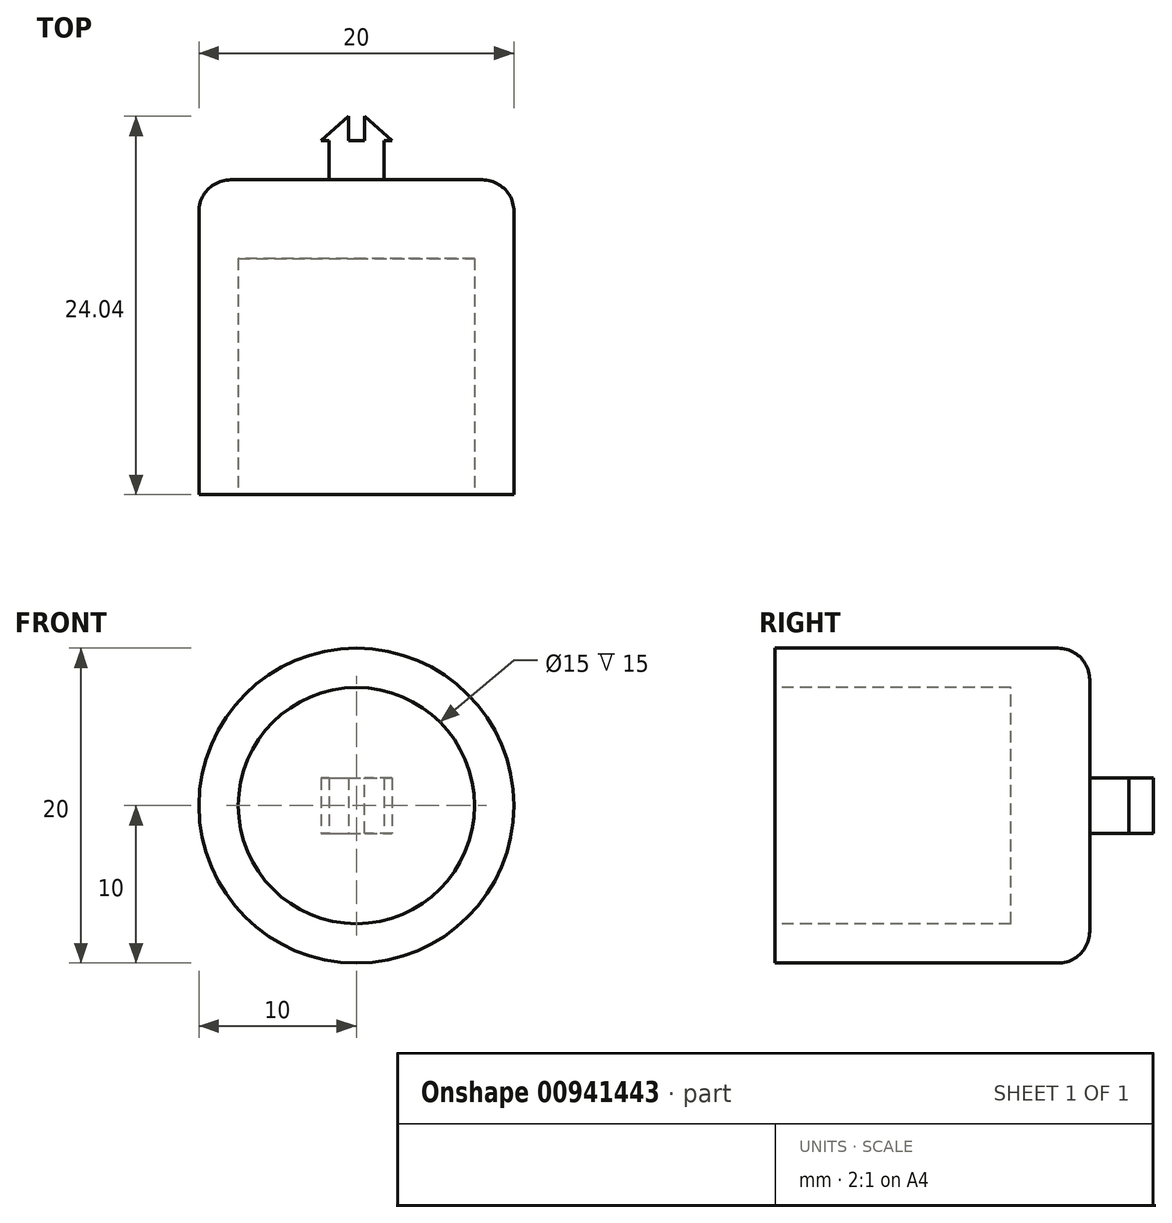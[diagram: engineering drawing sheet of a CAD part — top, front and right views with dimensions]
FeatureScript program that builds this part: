
annotation { "Feature Type Name" : "Feature", "Feature Type Description" : "" }
export const myFeature = defineFeature(function(context is Context, id is Id, definition is map)
    precondition{}
    {
        {
            var Q0;
            Q0=qCreatedBy(makeId("Top.planeOp"),FACE);
            var sketch = newSketch(context, id + "F0", { "sketchPlane" : qUnion([Q0])});
            skLineSegment(sketch, "E0", {"start": v(0, 0) * mm, "end": v(3.5, 0) * mm});
            skLineSegment(sketch, "E1", {"start": v(3.5, 0) * mm, "end": v(3.5, 2.5) * mm});
            skLineSegment(sketch, "E2", {"start": v(3.5, 2.5) * mm, "end": v(4, 2.5) * mm});
            skLineSegment(sketch, "E3", {"start": v(4, 2.5) * mm, "end": v(1.75, 4.48) * mm});
            skPoint(sketch, "E3.endSnap0", {"position": v(1.75, 0) * mm});
            skLineSegment(sketch, "E4", {"start": v(1.75, 4.48) * mm, "end": v(1.75, 0) * mm, "construction": true});
            skLineSegment(sketch, "E5.MirrorCS", {"start": v(-0.5, 2.5) * mm, "end": v(1.75, 4.48) * mm});
            skLineSegment(sketch, "E6.MirrorCS", {"start": v(0, 0) * mm, "end": v(0, 2.5) * mm});
            skLineSegment(sketch, "E7.MirrorCS", {"start": v(0, 2.5) * mm, "end": v(-0.5, 2.5) * mm});
            skSolve(sketch);
        }
        {
            var Q0;
            Q0 = qSketchRegion(id + "F0", true);
            extrude(context, id + "F1", {"entities" : qUnion([Q0]), "depth" : 3.5 * mm, "offsetDistance" : 25 * mm});
        }
        {
            var Q0;
            Q0=makeQuery(id+"F1.opExtrude","CAP_FACE",FACE,{"disambiguationData":[OSD([sQuery(id+"F0.wireOp",EDGE,"E0"),sQuery(id+"F0.wireOp",EDGE,"E1"),sQuery(id+"F0.wireOp",EDGE,"E2"),sQuery(id+"F0.wireOp",EDGE,"E3"),sQuery(id+"F0.wireOp",EDGE,"E5.MirrorCS"),sQuery(id+"F0.wireOp",EDGE,"E6.MirrorCS"),sQuery(id+"F0.wireOp",EDGE,"E7.MirrorCS")])],"isStart":false});
            var sketch = newSketch(context, id + "F2", { "sketchPlane" : qUnion([Q0])});
            skLineSegment(sketch, "E8.bottom", {"start": v(1.25, 2.5) * mm, "end": v(2.25, 2.5) * mm});
            skLineSegment(sketch, "E8.top", {"start": v(1.25, 6.47) * mm, "end": v(2.25, 6.47) * mm});
            skLineSegment(sketch, "E8.left", {"start": v(1.25, 2.5) * mm, "end": v(1.25, 6.47) * mm});
            skLineSegment(sketch, "E8.right", {"start": v(2.25, 2.5) * mm, "end": v(2.25, 6.47) * mm});
            skPoint(sketch, "E8.middle", {"position": v(1.75, 4.48) * mm});
            skSolve(sketch);
        }
        {
            var Q0;
            Q0 = qSketchRegion(id + "F2", true);
            var Q1;
            {var subQ1=sQuery(id+"F2.wireOp",EDGE,"E8.bottom");Q1=makeQuery(id+"F2.imprint","IMPRINT",FACE,{"disambiguationData":[TD([[makeQuery(id+"F2.imprint","IMPRINT",EDGE,{"derivedFrom":subQ1}),1.0]])]});}
            extrude(context, id + "F3", {"entities" : qUnion([Q0, Q1]), "operationType" : NewBodyOperationType.REMOVE, "oppositeDirection" : true, "depth" : 25 * mm, "offsetDistance" : 25 * mm});
        }
        {
            var Q0;
            Q0=makeQuery(id+"F1.opExtrude","SWEPT_FACE",FACE,{"disambiguationData":[OSD([sQuery(id+"F0.wireOp",EDGE,"E0")])]});
            var sketch = newSketch(context, id + "F4", { "sketchPlane" : qUnion([Q0])});
            skLineSegment(sketch, "E9", {"start": v(1.75, 3.5) * mm, "end": v(1.75, 1.75) * mm});
            skCircle(sketch, "E10", {"center": v(1.75, 1.75) * mm, "radius": 10 * mm});
            skSolve(sketch);
        }
        {
            var Q0;
            Q0 = qSketchRegion(id + "F4", true);
            extrude(context, id + "F5", {"entities" : qUnion([Q0]), "operationType" : NewBodyOperationType.ADD, "depth" : 20 * mm, "offsetDistance" : 25 * mm});
        }
        {
            var Q0;
            Q0=makeQuery(id+"F5.opExtrude","CAP_EDGE",EDGE,{"disambiguationData":[OSD([sQuery(id+"F4.wireOp",EDGE,"E10")])],"isStart":true});
            fillet(context, id + "F6", {"entities" : qUnion([Q0]), "radius" : 2 * mm, "tangentPropagation" : true, "allowEdgeOverflow" : false});
        }
        {
            var Q0;
            Q0=makeQuery(id+"F5.opExtrude","CAP_FACE",FACE,{"disambiguationData":[OSD([sQuery(id+"F4.wireOp",EDGE,"E10")])],"isStart":false});
            var sketch = newSketch(context, id + "F7", { "sketchPlane" : qUnion([Q0])});
            skCircle(sketch, "E11", {"center": v(1.75, 1.75) * mm, "radius": 7.5 * mm});
            skSolve(sketch);
        }
        {
            var Q0;
            Q0=makeQuery(id+"F7.imprint","IMPRINT",FACE,{"disambiguationData":[TD([[makeQuery(id+"F7.imprint","IMPRINT",EDGE,{"derivedFrom":sQuery(id+"F7.wireOp",EDGE,"E11")}),1.0]])]});
            extrude(context, id + "F8", {"entities" : qUnion([Q0]), "operationType" : NewBodyOperationType.REMOVE, "oppositeDirection" : true, "depth" : 15 * mm, "offsetDistance" : 25 * mm});
        }
    });
